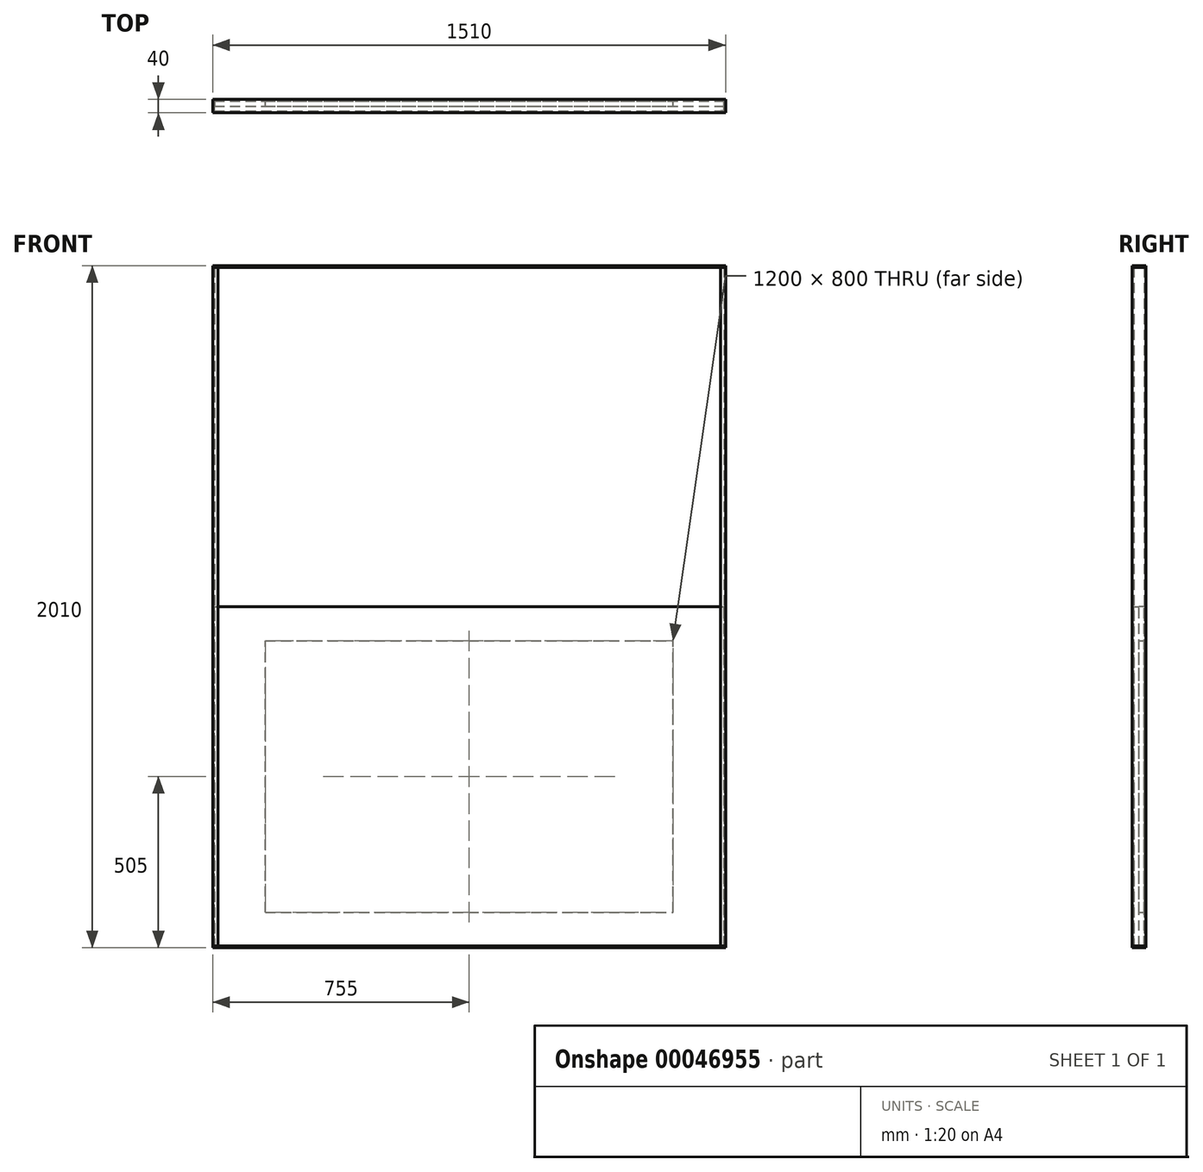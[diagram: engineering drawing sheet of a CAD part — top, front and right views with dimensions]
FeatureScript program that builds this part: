
annotation { "Feature Type Name" : "Feature", "Feature Type Description" : "" }
export const myFeature = defineFeature(function(context is Context, id is Id, definition is map)
    precondition{}
    {
        {
            var Q0;
            Q0=qCreatedBy(makeId("Top.planeOp"),FACE);
            var sketch = newSketch(context, id + "F0", { "sketchPlane" : qUnion([Q0])});
            skLineSegment(sketch, "E0", {"start": v(0, 0) * mm, "end": v(-750, 0) * mm, "construction": true});
            skLineSegment(sketch, "E1", {"start": v(-750, 0) * mm, "end": v(-750, -15) * mm});
            skLineSegment(sketch, "E2", {"start": v(-750, -15) * mm, "end": v(-740, -15) * mm});
            skLineSegment(sketch, "E3", {"start": v(-740, -15) * mm, "end": v(-740, -20) * mm});
            skLineSegment(sketch, "E4", {"start": v(-740, -20) * mm, "end": v(-755, -20) * mm});
            skLineSegment(sketch, "E5", {"start": v(-755, -20) * mm, "end": v(-755, 0) * mm});
            skLineSegment(sketch, "E6.MirrorCS", {"start": v(-740, 15) * mm, "end": v(-740, 20) * mm});
            skLineSegment(sketch, "E7.MirrorCS", {"start": v(-750, 15) * mm, "end": v(-740, 15) * mm});
            skLineSegment(sketch, "E8.MirrorCS", {"start": v(-750, 0) * mm, "end": v(-750, 15) * mm});
            skLineSegment(sketch, "E9.MirrorCS", {"start": v(-740, 20) * mm, "end": v(-755, 20) * mm});
            skLineSegment(sketch, "E10.MirrorCS", {"start": v(-755, 20) * mm, "end": v(-755, 0) * mm});
            skLineSegment(sketch, "E11.MirrorCS", {"start": v(740, -15) * mm, "end": v(740, -20) * mm});
            skLineSegment(sketch, "E12.MirrorCS", {"start": v(740, -20) * mm, "end": v(755, -20) * mm});
            skLineSegment(sketch, "E13.MirrorCS", {"start": v(755, -20) * mm, "end": v(755, 0) * mm});
            skLineSegment(sketch, "E14.MirrorCS", {"start": v(750, 0) * mm, "end": v(750, -15) * mm});
            skLineSegment(sketch, "E15.MirrorCS", {"start": v(750, -15) * mm, "end": v(740, -15) * mm});
            skLineSegment(sketch, "E16.MirrorCS", {"start": v(750, 15) * mm, "end": v(740, 15) * mm});
            skLineSegment(sketch, "E17.MirrorCS", {"start": v(750, 0) * mm, "end": v(750, 15) * mm});
            skLineSegment(sketch, "E18.MirrorCS", {"start": v(740, 15) * mm, "end": v(740, 20) * mm});
            skLineSegment(sketch, "E19.MirrorCS", {"start": v(740, 20) * mm, "end": v(755, 20) * mm});
            skLineSegment(sketch, "E20.MirrorCS", {"start": v(755, 20) * mm, "end": v(755, 0) * mm});
            skLineSegment(sketch, "E21.MirrorCS", {"start": v(0, 0) * mm, "end": v(750, 0) * mm, "construction": true});
            skSolve(sketch);
        }
        {
            var Q0;
            Q0=qSketchRegion(id+"F0",true);
            extrude(context, id + "F1", {"entities" : qUnion([Q0]), "depth" : 2000 * mm});
        }
        {
            var Q0;
            Q0=qCreatedBy(makeId("Front.planeOp"),FACE);
            var sketch = newSketch(context, id + "F2", { "sketchPlane" : qUnion([Q0])});
            skPoint(sketch, "E22.0", {"position": v(-750, 0) * mm});
            skLineSegment(sketch, "E23.bottom", {"start": v(-750, 0) * mm, "end": v(750, 0) * mm});
            skLineSegment(sketch, "E23.top", {"start": v(-750, 1000) * mm, "end": v(750, 1000) * mm});
            skLineSegment(sketch, "E23.left", {"start": v(-750, 0) * mm, "end": v(-750, 1000) * mm});
            skLineSegment(sketch, "E23.right", {"start": v(750, 0) * mm, "end": v(750, 1000) * mm});
            skSolve(sketch);
        }
        {
            var Q0;
            Q0=qSketchRegion(id+"F2",true);
            var Q1;
            Q1=makeQuery(id+"F2.imprint","IMPRINT",FACE,{"disambiguationData":[TD([[makeQuery(id+"F2.imprint","IMPRINT",EDGE,{"derivedFrom":sQuery(id+"F2.wireOp",EDGE,"E23.bottom")}),1.0]])]});
            extrude(context, id + "F3", {"entities" : qUnion([Q0, Q1]), "depth" : 15 * mm});
        }
        {
            var Q0;
            Q0=qSketchRegion(id+"F2",true);
            extrude(context, id + "F4", {"entities" : qUnion([Q0]), "oppositeDirection" : true, "depth" : 15 * mm});
        }
        {
            var Q0;
            Q0=makeQuery(id+"F1.opExtrude","CAP_FACE",FACE,{"disambiguationData":[OSD([sQuery(id+"F0.wireOp",EDGE,"E1"),sQuery(id+"F0.wireOp",EDGE,"E2"),sQuery(id+"F0.wireOp",EDGE,"E3"),sQuery(id+"F0.wireOp",EDGE,"E4"),sQuery(id+"F0.wireOp",EDGE,"E5"),sQuery(id+"F0.wireOp",EDGE,"E6.MirrorCS"),sQuery(id+"F0.wireOp",EDGE,"E7.MirrorCS"),sQuery(id+"F0.wireOp",EDGE,"E8.MirrorCS"),sQuery(id+"F0.wireOp",EDGE,"E9.MirrorCS"),sQuery(id+"F0.wireOp",EDGE,"E10.MirrorCS")])],"isStart":false});
            var sketch = newSketch(context, id + "F5", { "sketchPlane" : qUnion([Q0])});
            skLineSegment(sketch, "E24.bottom", {"start": v(-755, 20) * mm, "end": v(755, 20) * mm});
            skLineSegment(sketch, "E24.top", {"start": v(-755, -20) * mm, "end": v(755, -20) * mm});
            skLineSegment(sketch, "E24.left", {"start": v(-755, 20) * mm, "end": v(-755, -20) * mm});
            skLineSegment(sketch, "E24.right", {"start": v(755, 20) * mm, "end": v(755, -20) * mm});
            skLineSegment(sketch, "E25.MirrorCS", {"start": v(-755, -20) * mm, "end": v(-755, 20) * mm});
            skLineSegment(sketch, "E26.MirrorCS", {"start": v(755, -20) * mm, "end": v(755, 20) * mm});
            skSolve(sketch);
        }
        {
            var Q0;
            Q0=qSketchRegion(id+"F5",true);
            extrude(context, id + "F6", {"entities" : qUnion([Q0]), "depth" : 5 * mm});
        }
        {
            var Q0;
            Q0=makeQuery(id+"F0.imprint","IMPRINT",FACE,{"disambiguationData":[TD([[makeQuery(id+"F0.imprint","IMPRINT",EDGE,{"derivedFrom":sQuery(id+"F0.wireOp",EDGE,"E11.MirrorCS")}),1.0]])]});
            var sketch = newSketch(context, id + "F7", { "sketchPlane" : qUnion([Q0])});
            skLineSegment(sketch, "E27.bottom", {"start": v(755, 20) * mm, "end": v(-755, 20) * mm});
            skLineSegment(sketch, "E27.top", {"start": v(755, -20) * mm, "end": v(-755, -20) * mm});
            skLineSegment(sketch, "E27.left", {"start": v(755, 20) * mm, "end": v(755, -20) * mm});
            skLineSegment(sketch, "E27.right", {"start": v(-755, 20) * mm, "end": v(-755, -20) * mm});
            skSolve(sketch);
        }
        {
            var Q0;
            Q0=qSketchRegion(id+"F7",true);
            extrude(context, id + "F8", {"entities" : qUnion([Q0]), "oppositeDirection" : true, "depth" : 5 * mm});
        }
        {
            var Q0;
            Q0=makeQuery(id+"F4.opExtrude","CAP_FACE",FACE,{"disambiguationData":[OSD([sQuery(id+"F2.wireOp",EDGE,"E23.bottom"),sQuery(id+"F2.wireOp",EDGE,"E23.top"),sQuery(id+"F2.wireOp",EDGE,"E23.left"),sQuery(id+"F2.wireOp",EDGE,"E23.right")])],"isStart":false});
            var sketch = newSketch(context, id + "F9", { "sketchPlane" : qUnion([Q0])});
            skLineSegment(sketch, "E28", {"start": v(0, 100) * mm, "end": v(-600, 100) * mm});
            skLineSegment(sketch, "E29", {"start": v(-600, 100) * mm, "end": v(-600, 900) * mm});
            skLineSegment(sketch, "E30", {"start": v(-600, 900) * mm, "end": v(0, 900) * mm});
            skLineSegment(sketch, "E31.MirrorCS", {"start": v(600, 100) * mm, "end": v(600, 900) * mm});
            skLineSegment(sketch, "E32.MirrorCS", {"start": v(600, 900) * mm, "end": v(0, 900) * mm});
            skLineSegment(sketch, "E33.MirrorCS", {"start": v(0, 100) * mm, "end": v(600, 100) * mm});
            skSolve(sketch);
        }
        {
            var Q0;
            Q0=qSketchRegion(id+"F9",true);
            extrude(context, id + "F10", {"entities" : qUnion([Q0]), "operationType" : NewBodyOperationType.REMOVE, "oppositeDirection" : true, "depth" : 15 * mm});
        }
        {
            var Q0;
            Q0=makeQuery(id+"F4.opExtrude","CAP_FACE",FACE,{"disambiguationData":[OSD([sQuery(id+"F2.wireOp",EDGE,"E23.bottom"),sQuery(id+"F2.wireOp",EDGE,"E23.top"),sQuery(id+"F2.wireOp",EDGE,"E23.left"),sQuery(id+"F2.wireOp",EDGE,"E23.right")])],"isStart":false});
            var sketch = newSketch(context, id + "F11", { "sketchPlane" : qUnion([Q0])});
            skLineSegment(sketch, "E34.bottom", {"start": v(-600, 900) * mm, "end": v(600, 900) * mm});
            skLineSegment(sketch, "E34.top", {"start": v(-600, 100) * mm, "end": v(600, 100) * mm});
            skLineSegment(sketch, "E34.left", {"start": v(-600, 900) * mm, "end": v(-600, 100) * mm});
            skLineSegment(sketch, "E34.right", {"start": v(600, 900) * mm, "end": v(600, 100) * mm});
            skSolve(sketch);
        }
        {
            var Q0;
            Q0=qSketchRegion(id+"F11",true);
            extrude(context, id + "F12", {"entities" : qUnion([Q0]), "oppositeDirection" : true, "depth" : 15 * mm});
        }
    });
